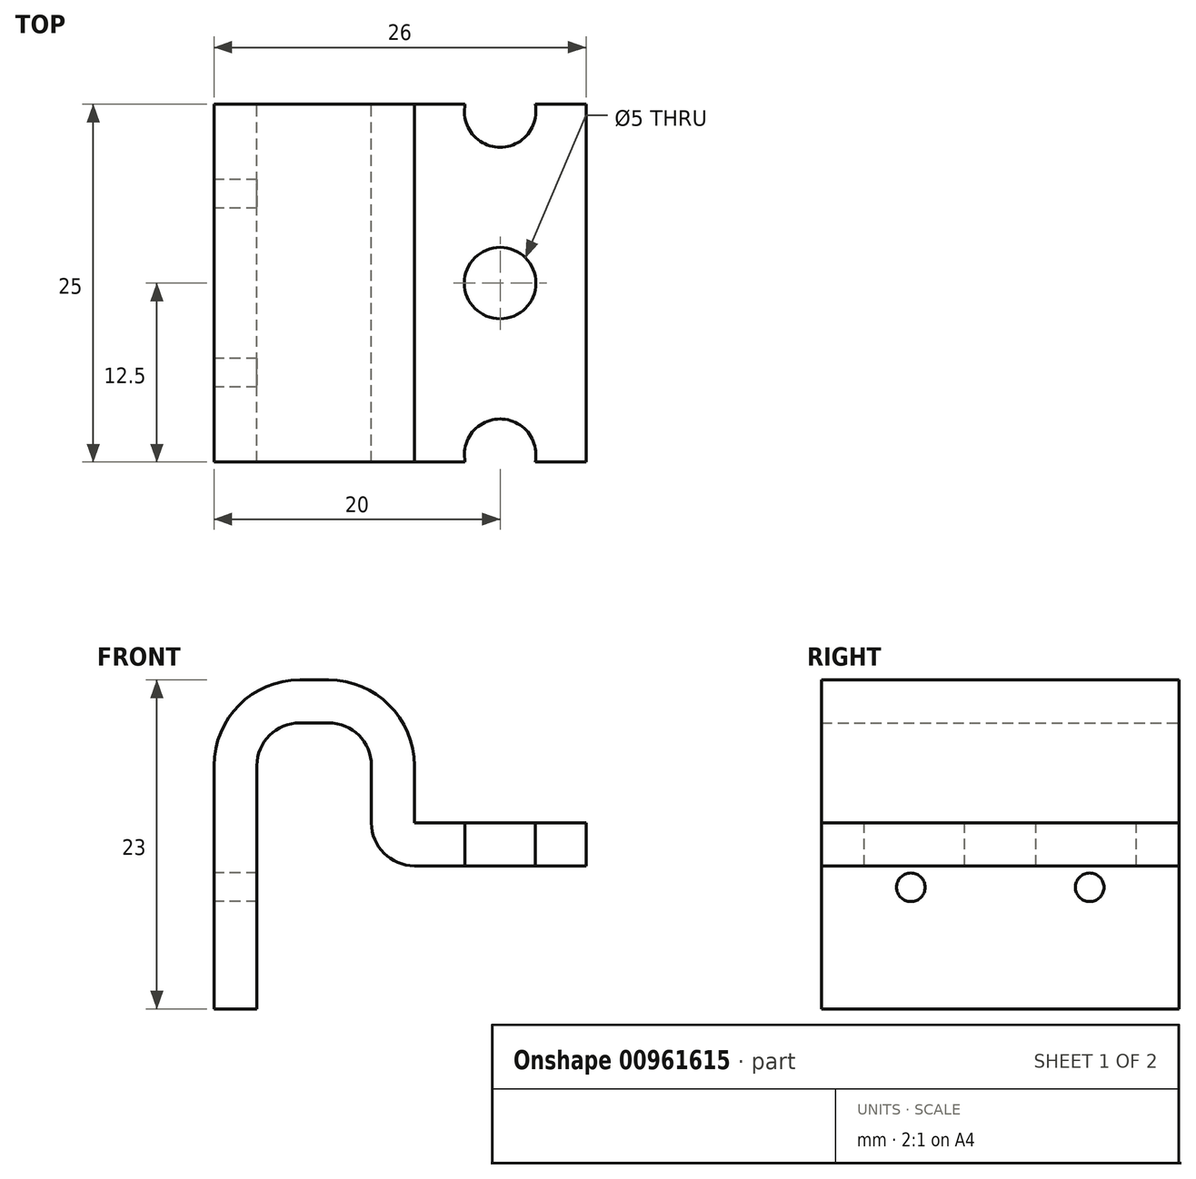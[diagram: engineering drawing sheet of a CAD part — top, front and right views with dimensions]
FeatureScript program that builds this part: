
annotation { "Feature Type Name" : "Feature", "Feature Type Description" : "" }
export const myFeature = defineFeature(function(context is Context, id is Id, definition is map)
    precondition{}
    {
        {
            var Q0;
            Q0=qCreatedBy(makeId("Front.planeOp"),FACE);
            var sketch = newSketch(context, id + "F0", { "sketchPlane" : qUnion([Q0])});
            skLineSegment(sketch, "E0", {"start": v(0, 0) * mm, "end": v(0, 17) * mm});
            skLineSegment(sketch, "E1", {"start": v(3, 20) * mm, "end": v(5, 20) * mm});
            skLineSegment(sketch, "E2", {"start": v(8, 17) * mm, "end": v(8, 13) * mm});
            skLineSegment(sketch, "E3", {"start": v(11, 10) * mm, "end": v(23, 10) * mm});
            skPoint(sketch, "E4.visualSharp", {"position": v(0, 20) * mm});
            skArc(sketch, "E4.filletArc", {"start": v(3, 20) * mm, "mid": v(0.88, 19.12) * mm, "end": v(0, 17) * mm});
            skPoint(sketch, "E5.visualSharp", {"position": v(8, 20) * mm});
            skArc(sketch, "E5.filletArc", {"start": v(8, 17) * mm, "mid": v(7.12, 19.12) * mm, "end": v(5, 20) * mm});
            skPoint(sketch, "E6.visualSharp", {"position": v(8, 10) * mm});
            skArc(sketch, "E6.filletArc", {"start": v(8, 13) * mm, "mid": v(8.88, 10.88) * mm, "end": v(11, 10) * mm});
            skArc(sketch, "E7.0", {"start": v(11, 17) * mm, "mid": v(9.24, 21.24) * mm, "end": v(5, 23) * mm});
            skLineSegment(sketch, "E7.1", {"start": v(3, 23) * mm, "end": v(5, 23) * mm});
            skArc(sketch, "E7.2", {"start": v(3, 23) * mm, "mid": v(-1.24, 21.24) * mm, "end": v(-3, 17) * mm});
            skLineSegment(sketch, "E7.3", {"start": v(-3, 0) * mm, "end": v(-3, 17) * mm});
            skLineSegment(sketch, "E8.0", {"start": v(11, 13) * mm, "end": v(23, 13) * mm});
            skLineSegment(sketch, "E8.1", {"start": v(11, 13) * mm, "end": v(11, 13) * mm});
            skLineSegment(sketch, "E8.2", {"start": v(11, 17) * mm, "end": v(11, 13) * mm});
            skLineSegment(sketch, "E9", {"start": v(23, 13) * mm, "end": v(23, 10) * mm});
            skLineSegment(sketch, "E10", {"start": v(-3, 0) * mm, "end": v(0, 0) * mm});
            skSolve(sketch);
        }
        {
            var Q0;
            Q0 = qSketchRegion(id + "F0", true);
            extrude(context, id + "F1", {"entities" : qUnion([Q0]), "depth" : 25 * mm, "offsetDistance" : 25 * mm});
        }
        {
            var Q0;
            Q0=makeQuery(id+"F1.opExtrude","SWEPT_FACE",FACE,{"disambiguationData":[OSD([sQuery(id+"F0.wireOp",EDGE,"E8.0")])]});
            var sketch = newSketch(context, id + "F2", { "sketchPlane" : qUnion([Q0])});
            skLineSegment(sketch, "E11", {"start": v(11, 0) * mm, "end": v(11, -25) * mm, "construction": true});
            skLineSegment(sketch, "E12", {"start": v(11, -25) * mm, "end": v(23, -25) * mm, "construction": true});
            skLineSegment(sketch, "E13", {"start": v(23, -25) * mm, "end": v(23, 0) * mm, "construction": true});
            skLineSegment(sketch, "E14", {"start": v(23, 0) * mm, "end": v(11, 0) * mm, "construction": true});
            skLineSegment(sketch, "E15", {"start": v(11, -12.5) * mm, "end": v(23, -12.5) * mm, "construction": true});
            skCircle(sketch, "E16", {"center": v(11, -12.5) * mm, "radius": 12 * mm, "construction": true});
            skLineSegment(sketch, "E17", {"start": v(11, -0.5) * mm, "end": v(23, -0.5) * mm, "construction": true});
            skLineSegment(sketch, "E18", {"start": v(11, -24.5) * mm, "end": v(23, -24.5) * mm, "construction": true});
            skCircle(sketch, "E19", {"center": v(17, -0.5) * mm, "radius": 2.5 * mm});
            skCircle(sketch, "E20", {"center": v(17, -12.5) * mm, "radius": 2.5 * mm});
            skCircle(sketch, "E21", {"center": v(17, -24.5) * mm, "radius": 2.5 * mm});
            skSolve(sketch);
        }
        {
            var Q0;
            Q0=makeQuery(id+"F2.imprint","IMPRINT",FACE,{"disambiguationData":[TD([[makeQuery(id+"F2.imprint","IMPRINT",EDGE,{"derivedFrom":sQuery(id+"F2.wireOp",EDGE,"E20")}),1.0]])]});
            var Q1;
            Q1=makeQuery(id+"F2.imprint","IMPRINT",FACE,{"disambiguationData":[TD([[makeQuery(id+"F2.imprint","IMPRINT",EDGE,{"derivedFrom":sQuery(id+"F2.wireOp",EDGE,"E21")}),1.0]])]});
            var Q2;
            Q2=makeQuery(id+"F2.imprint","IMPRINT",FACE,{"disambiguationData":[TD([[makeQuery(id+"F2.imprint","IMPRINT",EDGE,{"derivedFrom":sQuery(id+"F2.wireOp",EDGE,"E19")}),1.0]])]});
            extrude(context, id + "F3", {"entities" : qUnion([Q0, Q1, Q2]), "operationType" : NewBodyOperationType.REMOVE, "oppositeDirection" : true, "depth" : 25 * mm, "offsetDistance" : 25 * mm});
        }
        {
            var Q0;
            Q0=makeQuery(id+"F1.opExtrude","SWEPT_FACE",FACE,{"disambiguationData":[OSD([sQuery(id+"F0.wireOp",EDGE,"E7.3")])]});
            var sketch = newSketch(context, id + "F4", { "sketchPlane" : qUnion([Q0])});
            skLineSegment(sketch, "E22", {"start": v(0, 0) * mm, "end": v(12.5, 17) * mm, "construction": true});
            skLineSegment(sketch, "E23", {"start": v(12.5, 17) * mm, "end": v(25, 0) * mm, "construction": true});
            skCircle(sketch, "E24", {"center": v(6.25, 8.5) * mm, "radius": 1 * mm});
            skCircle(sketch, "E25", {"center": v(18.75, 8.5) * mm, "radius": 1 * mm});
            skSolve(sketch);
        }
        {
            var Q0;
            Q0=makeQuery(id+"F4.imprint","IMPRINT",FACE,{"disambiguationData":[TD([[makeQuery(id+"F4.imprint","IMPRINT",EDGE,{"derivedFrom":sQuery(id+"F4.wireOp",EDGE,"E25")}),1.0]])]});
            var Q1;
            Q1=makeQuery(id+"F4.imprint","IMPRINT",FACE,{"disambiguationData":[TD([[makeQuery(id+"F4.imprint","IMPRINT",EDGE,{"derivedFrom":sQuery(id+"F4.wireOp",EDGE,"E24")}),1.0]])]});
            extrude(context, id + "F5", {"entities" : qUnion([Q0, Q1]), "operationType" : NewBodyOperationType.REMOVE, "oppositeDirection" : true, "depth" : 5 * mm, "offsetDistance" : 25 * mm});
        }
    });
